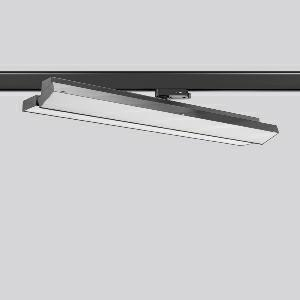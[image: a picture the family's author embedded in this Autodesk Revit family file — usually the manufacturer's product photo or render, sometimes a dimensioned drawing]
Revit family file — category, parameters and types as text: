
# Revit family: tx-move_742164_003_1_76_66b3
name_source: partatom
category: Lighting Fixtures
units: mm (PartAtom-declared; Revit-internal decimal feet)

## family parameters
Cut with Voids When Loaded = No
Host = Face
Light Source = No
Part Type = Normal
Room Calculation Point = No
Round Connector Dimension = Use Diameter
Shared = No

## types (1)
- MultiLumen 1 (1 x LED Modul 840, 2625 lm, 4000)
    Apparent Load = 41 VA
    CIE Flux Codes = 47 79 96 100 100
    Color Rendering = 80
    Color Temperature = 4000
    Default Elevation = 1800 mm
    Description = Series: TX-MOVE
Multifunctional surface-mounted spotlight for area lighting. Very flat design. Housing: sheet steel, powder-coated. Rotation range: 356°. Swivel range: 90°. Consistent alignment possible with visible tilt scale. High-efficiency LED units with flush-mounted opal diffuser made of non-yellowing PMMA. Symmetrical wide beam light emission. With adapter for RZB 3-circuit DALI tracks. Suitable for Track on ceiling. MultiLumen: Luminous flux adjustable in 3 steps. Factory setting is the highest luminous flux. Environmentally friendly and resource-saving due to replaceable and recyclable components. 
Colour: deep black, matt (RAL 9005)
Length: 570 mm
Width: 119 mm
Height: 88 mm
Lamp: LED
Socket: without socket
Colour temperature: 4000K
Colour rendering index (CRI): 80
System power: 41 W
Rated luminous flux: 5250 lm
Luminous efficiency: 128 lm/W
System power 2: 57 W
Rated luminous flux 2: 7150 lm
Luminous efficiency 2: 125 lm/W
System power 3: 73 W
Rated luminous flux 3: 8750 lm
Luminous efficiency 3: 120 lm/W
Control gear: Dimmable EVG, DALI
Protection class: I
Type of protection: IP 20
    Height = 75 mm
    Lamp = 1 x LED Modul 840
    Lamp Light Flux = 2625 lm
    Lamp count = 1
    Length = 569 mm
    Lifetime = 50000 h
    Luminous efficacy = 128 lm/W
    Manufacturer = RZB
    ModVariant = No
    Model = 742164.003.1.76
    Mounting Place = Ceiling
    Mounting Type = Surface mounted
    Number of Poles = 1
    OnlyDefault = Yes
    Power Factor = 1
    Product Name = TX-MOVE
    Product group = Track mounted projectors
    ProductGroupID = 301
    Protection Class = Protection class I
    Protection Degree = IP 20
    RLX_Detail_Level = 1
    RLX_Emergency_Light_Flux = 0 lm
    RLX_Emergency_Type = 0
    RLX_Emergency_Type_DB = No
    RlxData = <blob elided: 35565 chars, md5=6c4cc0f4>
    Socket = socket
    Standby Power = 0 W
    System Light Flux = 5250 lm
    System Power = 41 W
    Type Comments = MultiLumen 1
    Type Image = 742164.003.jpg
    URL = http://relux.com
    VarID = multilumen_1
    Voltage = 0 V
    Weight = 0.00 kg
    Width = 119 mm

## geometry (parser evidence)
native form markers: Blend x4, Sweep x15
no freeform markers — native parametric forms only
